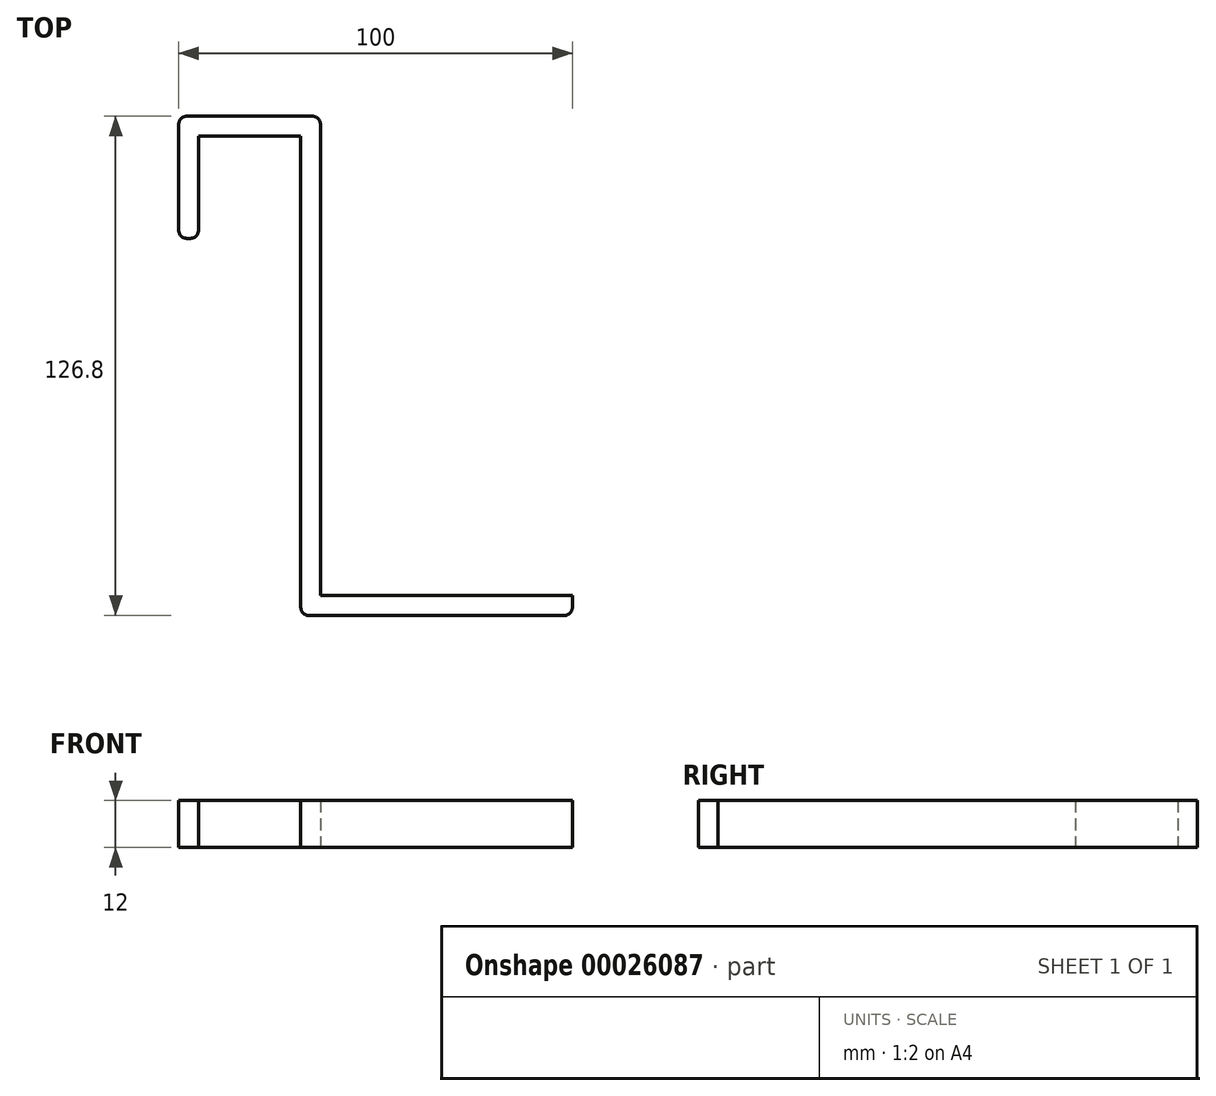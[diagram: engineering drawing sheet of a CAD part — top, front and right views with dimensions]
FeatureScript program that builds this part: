
annotation { "Feature Type Name" : "Feature", "Feature Type Description" : "" }
export const myFeature = defineFeature(function(context is Context, id is Id, definition is map)
    precondition{}
    {
        {
            var Q0;
            Q0=qCreatedBy(makeId("Top.planeOp"),FACE);
            var sketch = newSketch(context, id + "F0", { "sketchPlane" : qUnion([Q0])});
            skLineSegment(sketch, "E0", {"start": v(-26.55, 16.72) * mm, "end": v(-26.55, 40.72) * mm});
            skLineSegment(sketch, "E1", {"start": v(-26.55, 40.72) * mm, "end": v(-0.55, 40.72) * mm});
            skLineSegment(sketch, "E2", {"start": v(-0.55, 40.72) * mm, "end": v(-0.55, -79.08) * mm});
            skLineSegment(sketch, "E3", {"start": v(4.45, -76.08) * mm, "end": v(68.45, -76.08) * mm});
            skLineSegment(sketch, "E4.0", {"start": v(-31.55, 16.72) * mm, "end": v(-31.55, 43.72) * mm});
            skLineSegment(sketch, "E5.0", {"start": v(-29.55, 45.72) * mm, "end": v(2.45, 45.72) * mm});
            skLineSegment(sketch, "E6.0", {"start": v(4.45, 43.72) * mm, "end": v(4.45, -76.08) * mm});
            skLineSegment(sketch, "E7.0", {"start": v(1.45, -81.08) * mm, "end": v(66.45, -81.08) * mm});
            skLineSegment(sketch, "E8", {"start": v(68.45, -76.08) * mm, "end": v(68.45, -79.08) * mm});
            skPoint(sketch, "E9.orphan", {"position": v(-0.55, -76.08) * mm});
            skLineSegment(sketch, "E10", {"start": v(-29.55, 14.72) * mm, "end": v(-28.55, 14.72) * mm});
            skPoint(sketch, "E11.visualSharp", {"position": v(-31.55, 14.72) * mm});
            skArc(sketch, "E11.filletArc", {"start": v(-31.55, 16.72) * mm, "mid": v(-30.96, 15.3) * mm, "end": v(-29.55, 14.72) * mm});
            skPoint(sketch, "E12.visualSharp", {"position": v(-26.55, 14.72) * mm});
            skArc(sketch, "E12.filletArc", {"start": v(-28.55, 14.72) * mm, "mid": v(-27.14, 15.3) * mm, "end": v(-26.55, 16.72) * mm});
            skPoint(sketch, "E13.visualSharp", {"position": v(-31.55, 45.72) * mm});
            skArc(sketch, "E13.filletArc", {"start": v(-29.55, 45.72) * mm, "mid": v(-30.96, 45.13) * mm, "end": v(-31.55, 43.72) * mm});
            skPoint(sketch, "E14.visualSharp", {"position": v(4.45, 45.72) * mm});
            skArc(sketch, "E14.filletArc", {"start": v(4.45, 43.72) * mm, "mid": v(3.86, 45.13) * mm, "end": v(2.45, 45.72) * mm});
            skPoint(sketch, "E15.visualSharp", {"position": v(-0.55, -81.08) * mm});
            skArc(sketch, "E15.filletArc", {"start": v(-0.55, -79.08) * mm, "mid": v(0.04, -80.5) * mm, "end": v(1.45, -81.08) * mm});
            skPoint(sketch, "E16.visualSharp", {"position": v(68.45, -81.08) * mm});
            skArc(sketch, "E16.filletArc", {"start": v(66.45, -81.08) * mm, "mid": v(67.86, -80.5) * mm, "end": v(68.45, -79.08) * mm});
            skPoint(sketch, "E17.visualSharp", {"position": v(68.45, -76.08) * mm});
            skSolve(sketch);
        }
        {
            var Q0;
            Q0=makeQuery(id+"F0.imprint","IMPRINT",FACE,{"disambiguationData":[TD([[makeQuery(id+"F0.imprint","IMPRINT",EDGE,{"derivedFrom":sQuery(id+"F0.wireOp",EDGE,"E0")}),1.0]])]});
            extrude(context, id + "F1", {"entities" : qUnion([Q0]), "depth" : 12 * mm});
        }
    });
